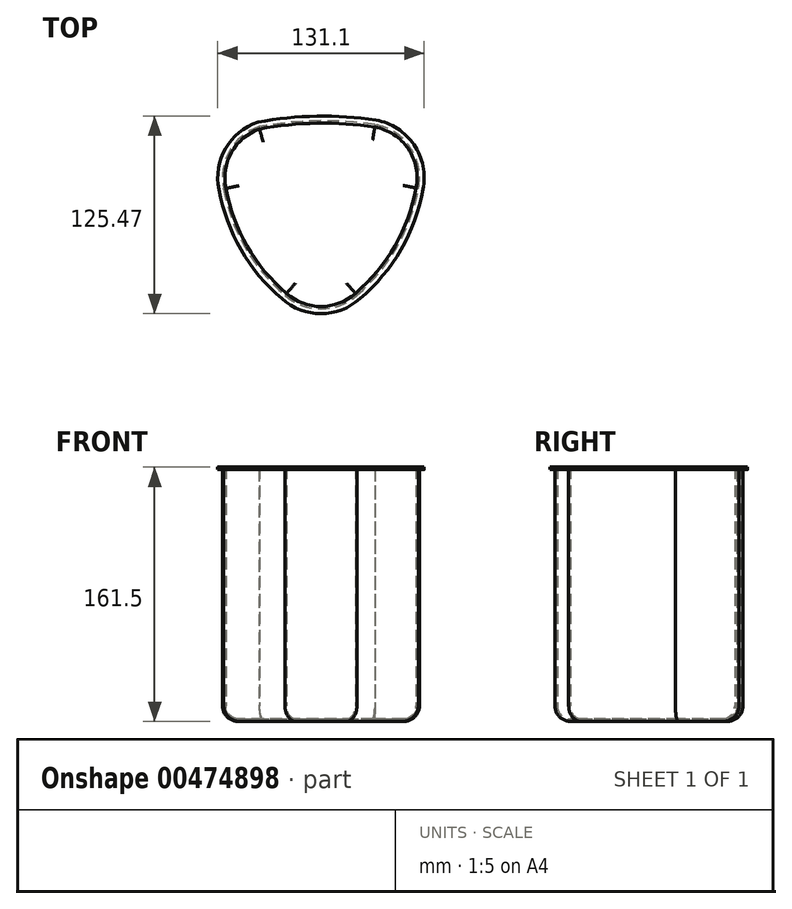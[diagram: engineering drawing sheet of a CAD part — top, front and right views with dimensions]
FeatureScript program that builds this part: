
annotation { "Feature Type Name" : "Feature", "Feature Type Description" : "" }
export const myFeature = defineFeature(function(context is Context, id is Id, definition is map)
    precondition{}
    {
        {
            var Q0;
            Q0=qCreatedBy(makeId("Top.planeOp"),FACE);
            var sketch = newSketch(context, id + "F0", { "sketchPlane" : qUnion([Q0])});
            skArc(sketch, "E0.0", {"start": v(66.8, 13.5) * mm, "mid": v(60.8, 43.29) * mm, "end": v(35.27, 59.78) * mm});
            skArc(sketch, "E0.1", {"start": v(-26.09, -57.1) * mm, "mid": v(0.03, -67.1) * mm, "end": v(26.14, -57.1) * mm});
            skArc(sketch, "E0.4", {"start": v(-40.56, 58.44) * mm, "mid": v(-62.28, 40.82) * mm, "end": v(-66.68, 13.2) * mm});
            skPoint(sketch, "E1.endSnap0", {"position": v(0.03, -67.1) * mm});
            skArc(sketch, "E2", {"start": v(26.14, -57.1) * mm, "mid": v(52.65, -25.36) * mm, "end": v(66.8, 13.5) * mm});
            skArc(sketch, "E3", {"start": v(-66.68, 13.2) * mm, "mid": v(-52.5, -25.49) * mm, "end": v(-26.09, -57.1) * mm});
            skArc(sketch, "E4", {"start": v(35.27, 59.78) * mm, "mid": v(-2.7, 62.33) * mm, "end": v(-40.56, 58.44) * mm});
            skArc(sketch, "E5.0", {"start": v(22.86, -53.34) * mm, "mid": v(48.31, -22.87) * mm, "end": v(61.89, 14.44) * mm});
            skArc(sketch, "E5.1", {"start": v(34.46, 54.84) * mm, "mid": v(-2.48, 57.33) * mm, "end": v(-39.3, 53.59) * mm});
            skArc(sketch, "E5.2", {"start": v(-39.3, 53.59) * mm, "mid": v(-58.05, 38.15) * mm, "end": v(-61.77, 14.17) * mm});
            skArc(sketch, "E5.3", {"start": v(61.89, 14.44) * mm, "mid": v(56.7, 40.43) * mm, "end": v(34.46, 54.84) * mm});
            skArc(sketch, "E5.4", {"start": v(-61.77, 14.17) * mm, "mid": v(-48.18, -22.99) * mm, "end": v(-22.8, -53.34) * mm});
            skArc(sketch, "E5.5", {"start": v(-22.8, -53.34) * mm, "mid": v(0.03, -62.1) * mm, "end": v(22.86, -53.34) * mm});
            skSolve(sketch);
        }
        {
            var Q0;
            Q0=makeQuery(id+"F0.imprint","IMPRINT",FACE,{"disambiguationData":[TD([[makeQuery(id+"F0.imprint","IMPRINT",EDGE,{"derivedFrom":sQuery(id+"F0.wireOp",EDGE,"E5.0")}),1.0]])]});
            extrude(context, id + "F1", {"entities" : qUnion([Q0]), "depth" : 160 * mm});
        }
        {
            var Q0;
            Q0=makeQuery(id+"F1.opExtrude","CAP_FACE",FACE,{"disambiguationData":[OSD([sQuery(id+"F0.wireOp",EDGE,"E5.0"),sQuery(id+"F0.wireOp",EDGE,"E5.1"),sQuery(id+"F0.wireOp",EDGE,"E5.2"),sQuery(id+"F0.wireOp",EDGE,"E5.3"),sQuery(id+"F0.wireOp",EDGE,"E5.4"),sQuery(id+"F0.wireOp",EDGE,"E5.5")])],"isStart":false});
            var sketch = newSketch(context, id + "F2", { "sketchPlane" : qUnion([Q0])});
            skArc(sketch, "E6.0", {"start": v(66.79, 13.48) * mm, "mid": v(60.78, 43.26) * mm, "end": v(35.26, 59.75) * mm});
            skArc(sketch, "E6.1", {"start": v(-26.1, -57.13) * mm, "mid": v(0.02, -67.13) * mm, "end": v(26.13, -57.13) * mm});
            skArc(sketch, "E6.4", {"start": v(-40.58, 58.41) * mm, "mid": v(-62.3, 40.8) * mm, "end": v(-66.7, 13.18) * mm});
            skPoint(sketch, "E7.endSnap0", {"position": v(0.02, -67.13) * mm});
            skArc(sketch, "E8", {"start": v(26.13, -57.13) * mm, "mid": v(52.64, -25.38) * mm, "end": v(66.79, 13.48) * mm});
            skArc(sketch, "E9", {"start": v(-66.7, 13.18) * mm, "mid": v(-52.52, -25.51) * mm, "end": v(-26.1, -57.13) * mm});
            skArc(sketch, "E10", {"start": v(35.26, 59.75) * mm, "mid": v(-2.72, 62.3) * mm, "end": v(-40.58, 58.41) * mm});
            skArc(sketch, "E11.0", {"start": v(34.93, 57.78) * mm, "mid": v(-2.63, 60.3) * mm, "end": v(-40.08, 56.47) * mm});
            skArc(sketch, "E11.1", {"start": v(-64.73, 13.56) * mm, "mid": v(-50.8, -24.51) * mm, "end": v(-24.78, -55.62) * mm});
            skArc(sketch, "E11.2", {"start": v(-24.78, -55.62) * mm, "mid": v(0.02, -65.13) * mm, "end": v(24.82, -55.62) * mm});
            skArc(sketch, "E11.3", {"start": v(-40.08, 56.47) * mm, "mid": v(-60.6, 39.73) * mm, "end": v(-64.73, 13.56) * mm});
            skArc(sketch, "E11.4", {"start": v(24.82, -55.62) * mm, "mid": v(50.9, -24.38) * mm, "end": v(64.82, 13.86) * mm});
            skArc(sketch, "E11.5", {"start": v(64.82, 13.86) * mm, "mid": v(59.14, 42.12) * mm, "end": v(34.93, 57.78) * mm});
            skSolve(sketch);
        }
        {
            var Q0;
            Q0=makeQuery(id+"F1.opExtrude","CAP_FACE",FACE,{"disambiguationData":[OSD([sQuery(id+"F0.wireOp",EDGE,"E5.0"),sQuery(id+"F0.wireOp",EDGE,"E5.1"),sQuery(id+"F0.wireOp",EDGE,"E5.2"),sQuery(id+"F0.wireOp",EDGE,"E5.3"),sQuery(id+"F0.wireOp",EDGE,"E5.4"),sQuery(id+"F0.wireOp",EDGE,"E5.5")])],"isStart":true});
            fillet(context, id + "F3", {"entities" : qUnion([Q0]), "radius" : 10 * mm, "tangentPropagation" : true, "allowEdgeOverflow" : false});
        }
        {
            var Q0;
            Q0=makeQuery(id+"F1.opExtrude","CAP_FACE",FACE,{"disambiguationData":[OSD([sQuery(id+"F0.wireOp",EDGE,"E5.0"),sQuery(id+"F0.wireOp",EDGE,"E5.1"),sQuery(id+"F0.wireOp",EDGE,"E5.2"),sQuery(id+"F0.wireOp",EDGE,"E5.3"),sQuery(id+"F0.wireOp",EDGE,"E5.4"),sQuery(id+"F0.wireOp",EDGE,"E5.5")])],"isStart":false});
            shell(context, id + "F4", {"entities" : qUnion([Q0]), "thickness" : 1.5 * mm});
        }
        {
            var Q0;
            Q0=makeQuery(id+"F2.imprint","IMPRINT",FACE,{"disambiguationData":[TD([[makeQuery(id+"F2.imprint","IMPRINT",EDGE,{"derivedFrom":sQuery(id+"F2.wireOp",EDGE,"E11.0")}),1.0]])]});
            extrude(context, id + "F5", {"entities" : qUnion([Q0]), "operationType" : NewBodyOperationType.ADD, "depth" : 1.5 * mm});
        }
        {
            var Q0;
            Q0=makeQuery(id+"F1.opExtrude","CAP_FACE",FACE,{"disambiguationData":[OSD([sQuery(id+"F0.wireOp",EDGE,"E5.0"),sQuery(id+"F0.wireOp",EDGE,"E5.1"),sQuery(id+"F0.wireOp",EDGE,"E5.2"),sQuery(id+"F0.wireOp",EDGE,"E5.3"),sQuery(id+"F0.wireOp",EDGE,"E5.4"),sQuery(id+"F0.wireOp",EDGE,"E5.5")])],"isStart":false});
            extrude(context, id + "F6", {"entities" : qUnion([Q0]), "operationType" : NewBodyOperationType.ADD, "depth" : 1.5 * mm});
        }
    });
